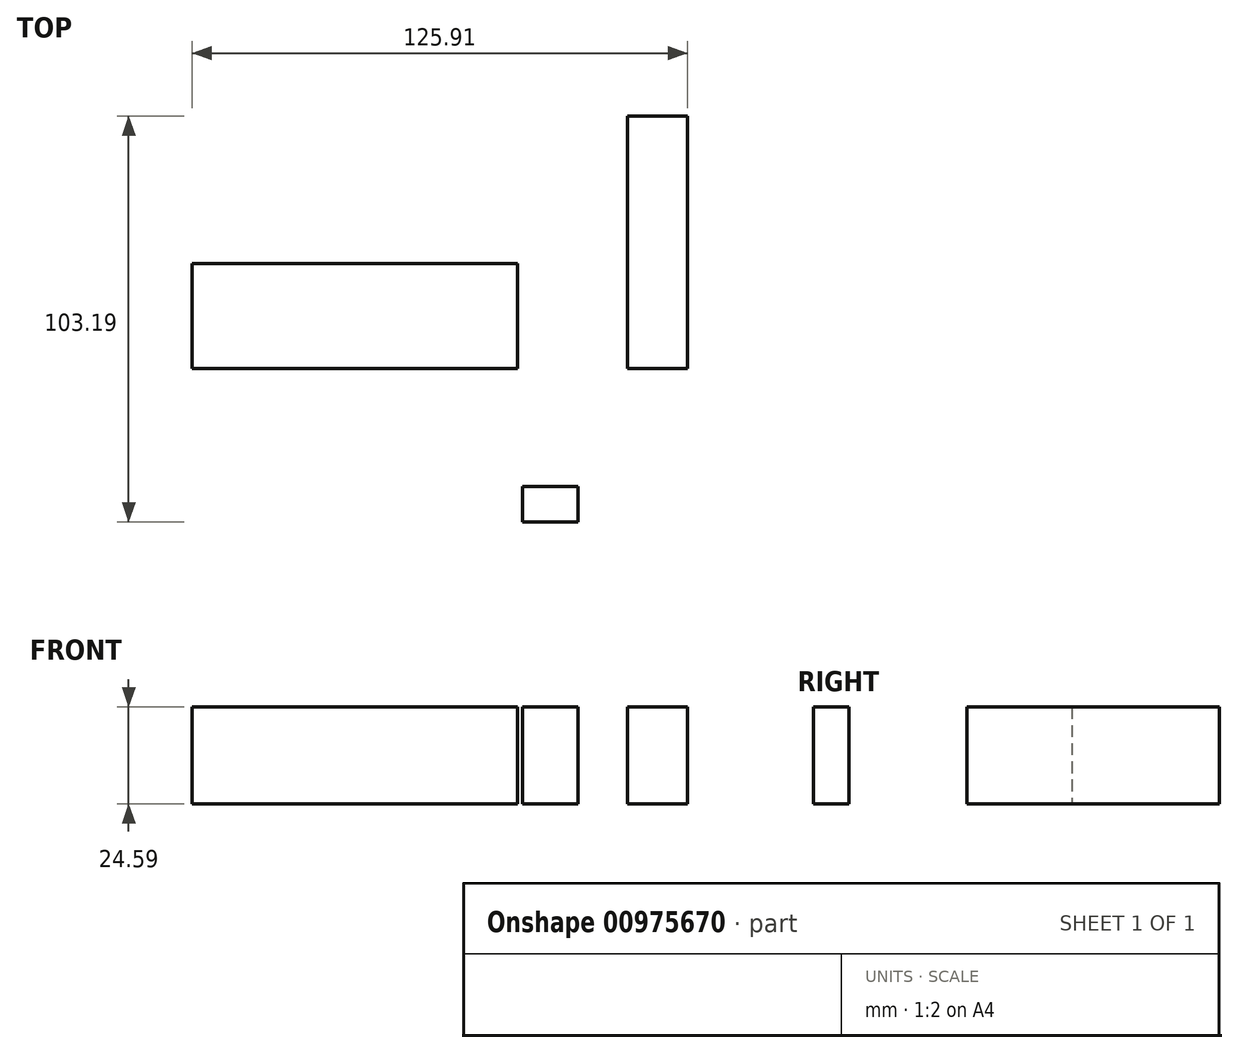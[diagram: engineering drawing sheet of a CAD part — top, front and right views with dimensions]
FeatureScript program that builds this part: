
annotation { "Feature Type Name" : "Feature", "Feature Type Description" : "" }
export const myFeature = defineFeature(function(context is Context, id is Id, definition is map)
    precondition{}
    {
        {
            var Q0;
            Q0=qCreatedBy(makeId("Top.planeOp"),FACE);
            var sketch = newSketch(context, id + "F0", { "sketchPlane" : qUnion([Q0])});
            skLineSegment(sketch, "E0.bottom", {"start": v(38.94, 14.8) * mm, "end": v(-43.78, 14.8) * mm});
            skLineSegment(sketch, "E0.top", {"start": v(38.94, 41.54) * mm, "end": v(-43.78, 41.54) * mm});
            skLineSegment(sketch, "E0.left", {"start": v(38.94, 14.8) * mm, "end": v(38.94, 41.54) * mm});
            skLineSegment(sketch, "E0.right", {"start": v(-43.78, 14.8) * mm, "end": v(-43.78, 41.54) * mm});
            skLineSegment(sketch, "E1.bottom", {"start": v(82.13, 79.02) * mm, "end": v(66.83, 79.02) * mm});
            skLineSegment(sketch, "E1.top", {"start": v(82.13, 14.8) * mm, "end": v(66.83, 14.8) * mm});
            skLineSegment(sketch, "E1.left", {"start": v(82.13, 79.02) * mm, "end": v(82.13, 14.8) * mm});
            skLineSegment(sketch, "E1.right", {"start": v(66.83, 79.02) * mm, "end": v(66.83, 14.8) * mm});
            skLineSegment(sketch, "E2.bottom", {"start": v(54.29, -15.14) * mm, "end": v(40.17, -15.14) * mm});
            skLineSegment(sketch, "E2.top", {"start": v(54.29, -24.17) * mm, "end": v(40.17, -24.17) * mm});
            skLineSegment(sketch, "E2.left", {"start": v(54.29, -15.14) * mm, "end": v(54.29, -24.17) * mm});
            skLineSegment(sketch, "E2.right", {"start": v(40.17, -15.14) * mm, "end": v(40.17, -24.17) * mm});
            skPoint(sketch, "E3", {"position": v(54.48, -59.39) * mm});
            skPoint(sketch, "E4", {"position": v(-47.98, -24.17) * mm});
            skPoint(sketch, "E5", {"position": v(0, -24.17) * mm});
            skPoint(sketch, "E6", {"position": v(13.92, 14.8) * mm});
            skPoint(sketch, "E7", {"position": v(34.51, 76.59) * mm});
            skPoint(sketch, "E8", {"position": v(0, 26.47) * mm});
            skPoint(sketch, "E9", {"position": v(72.94, 0) * mm});
            skPoint(sketch, "E10", {"position": v(40.17, -15.14) * mm});
            skPoint(sketch, "E11", {"position": v(39.83, 20) * mm});
            skSolve(sketch);
        }
        {
            var Q0;
            Q0 = qSketchRegion(id + "F0", true);
            extrude(context, id + "F1", {"entities" : qUnion([Q0]), "depth" : 24.59 * mm, "offsetDistance" : 25.4 * mm});
        }
    });
